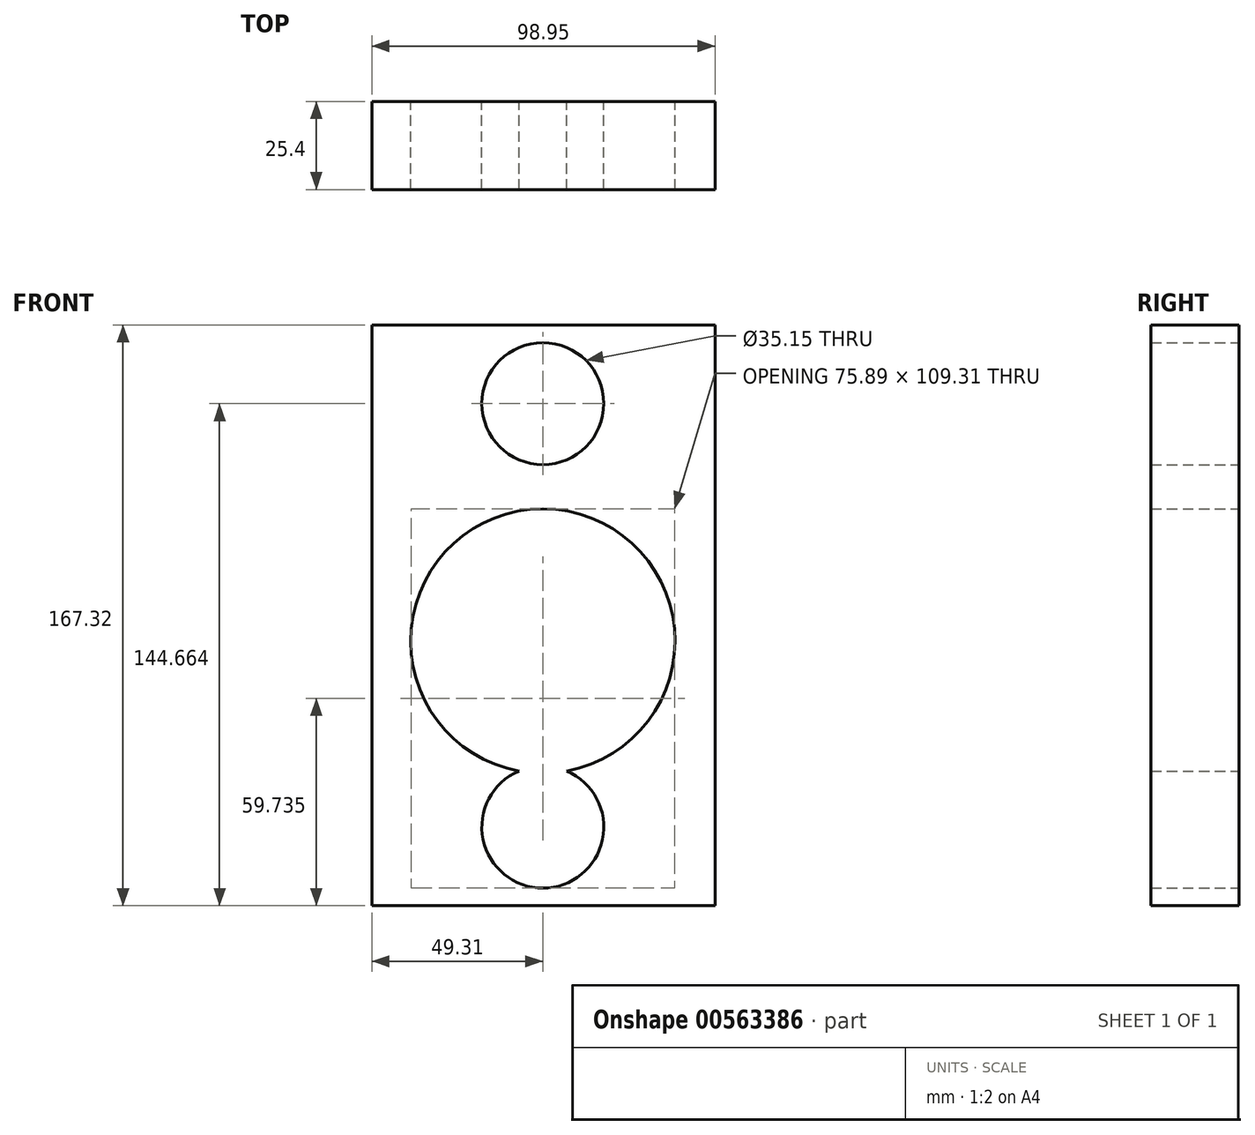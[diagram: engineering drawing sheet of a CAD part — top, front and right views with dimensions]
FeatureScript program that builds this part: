
annotation { "Feature Type Name" : "Feature", "Feature Type Description" : "" }
export const myFeature = defineFeature(function(context is Context, id is Id, definition is map)
    precondition{}
    {
        {
            var Q0;
            Q0=qCreatedBy(makeId("Front.planeOp"),FACE);
            var sketch = newSketch(context, id + "F0", { "sketchPlane" : qUnion([Q0])});
            skCircle(sketch, "E0", {"center": v(0, 0) * mm, "radius": 38.1 * mm});
            skCircle(sketch, "E1", {"center": v(0, 68.37) * mm, "radius": 17.57 * mm});
            skCircle(sketch, "E2", {"center": v(0, -53.64) * mm, "radius": 17.57 * mm});
            skLineSegment(sketch, "E3.bottom", {"start": v(-49.3, 91.03) * mm, "end": v(49.64, 91.03) * mm});
            skLineSegment(sketch, "E3.top", {"start": v(-49.3, -76.3) * mm, "end": v(49.64, -76.3) * mm});
            skLineSegment(sketch, "E3.left", {"start": v(-49.3, 91.03) * mm, "end": v(-49.3, -76.3) * mm});
            skLineSegment(sketch, "E3.right", {"start": v(49.64, 91.03) * mm, "end": v(49.64, -76.3) * mm});
            skSolve(sketch);
        }
        {
            var Q0;
            Q0 = qSketchRegion(id + "F0", true);
            extrude(context, id + "F1", {"entities" : qUnion([Q0]), "depth" : 25.4 * mm, "offsetDistance" : 25.4 * mm});
        }
    });
